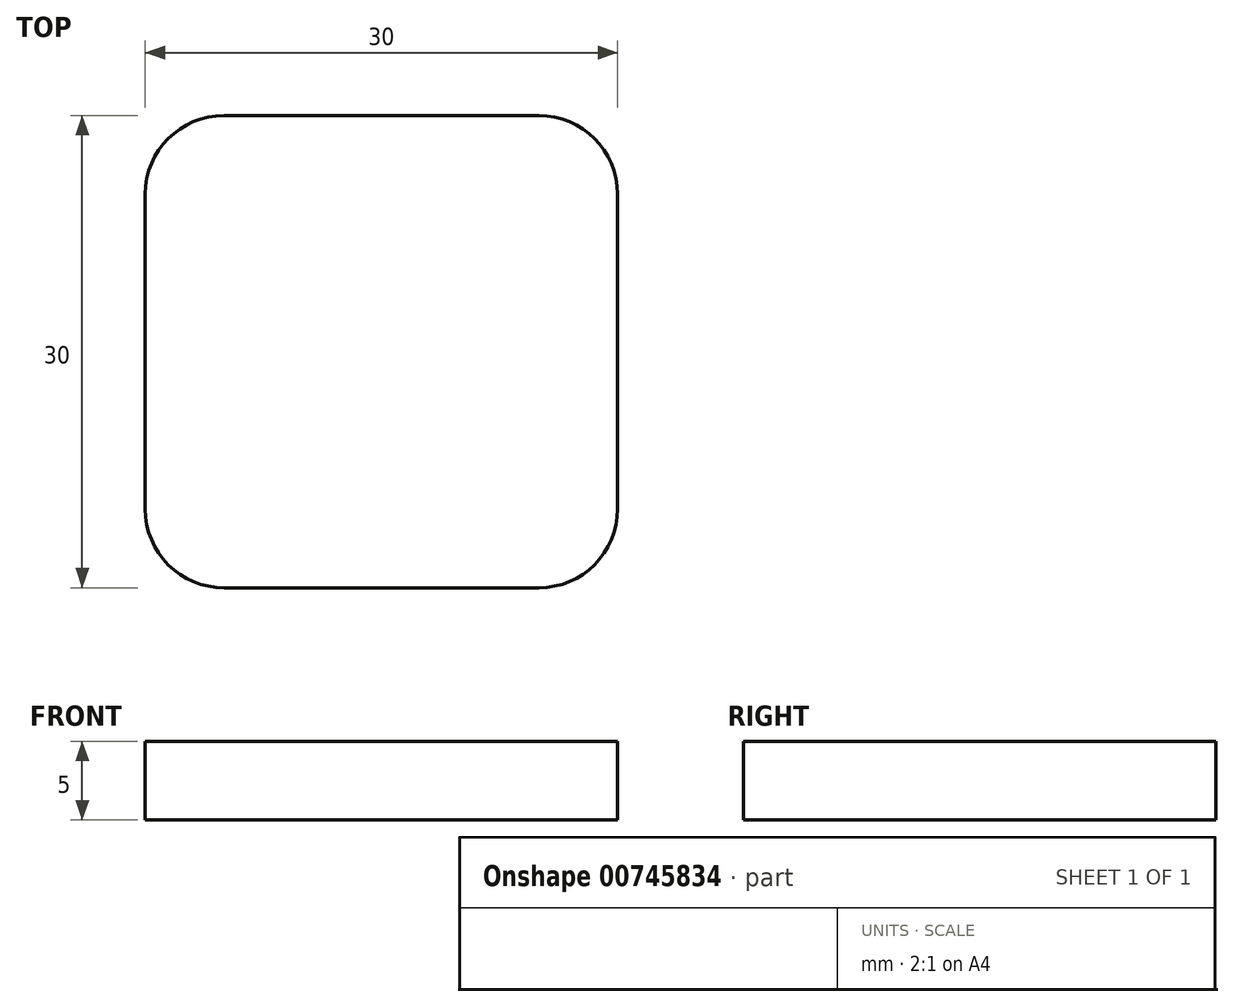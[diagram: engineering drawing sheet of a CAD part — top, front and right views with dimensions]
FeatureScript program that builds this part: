
annotation { "Feature Type Name" : "Feature", "Feature Type Description" : "" }
export const myFeature = defineFeature(function(context is Context, id is Id, definition is map)
    precondition{}
    {
        {
            var Q0;
            Q0=qCreatedBy(makeId("Top.planeOp"),FACE);
            var sketch = newSketch(context, id + "F0", { "sketchPlane" : qUnion([Q0])});
            skLineSegment(sketch, "E0.bottom", {"start": v(10, -15) * mm, "end": v(-10, -15) * mm});
            skLineSegment(sketch, "E0.top", {"start": v(10, 15) * mm, "end": v(-10, 15) * mm});
            skLineSegment(sketch, "E0.left", {"start": v(15, -10) * mm, "end": v(15, 10) * mm});
            skLineSegment(sketch, "E0.right", {"start": v(-15, -10) * mm, "end": v(-15, 10) * mm});
            skPoint(sketch, "E0.middle", {"position": v(0, 0) * mm});
            skPoint(sketch, "E1.visualSharp", {"position": v(-15, 15) * mm});
            skArc(sketch, "E1.filletArc", {"start": v(-10, 15) * mm, "mid": v(-13.54, 13.54) * mm, "end": v(-15, 10) * mm});
            skPoint(sketch, "E2.visualSharp", {"position": v(15, 15) * mm});
            skArc(sketch, "E2.filletArc", {"start": v(15, 10) * mm, "mid": v(13.54, 13.54) * mm, "end": v(10, 15) * mm});
            skPoint(sketch, "E3.visualSharp", {"position": v(15, -15) * mm});
            skArc(sketch, "E3.filletArc", {"start": v(10, -15) * mm, "mid": v(13.54, -13.54) * mm, "end": v(15, -10) * mm});
            skPoint(sketch, "E4.visualSharp", {"position": v(-15, -15) * mm});
            skArc(sketch, "E4.filletArc", {"start": v(-15, -10) * mm, "mid": v(-13.54, -13.54) * mm, "end": v(-10, -15) * mm});
            skSolve(sketch);
        }
        {
            var Q0;
            Q0 = qSketchRegion(id + "F0", true);
            extrude(context, id + "F1", {"entities" : qUnion([Q0]), "depth" : 5 * mm, "offsetDistance" : 25 * mm});
        }
    });
